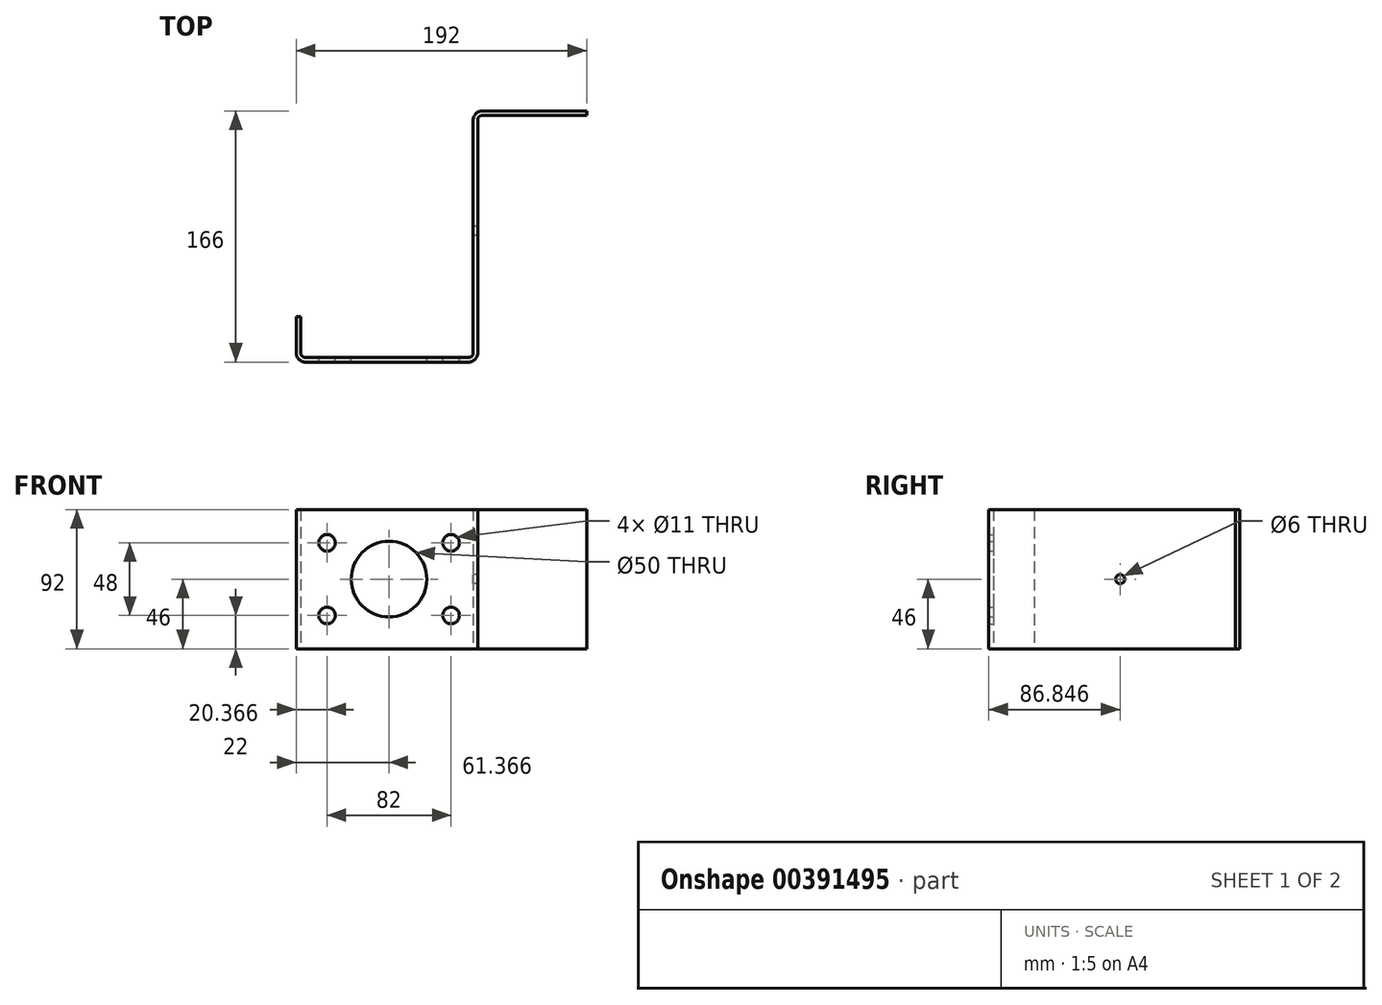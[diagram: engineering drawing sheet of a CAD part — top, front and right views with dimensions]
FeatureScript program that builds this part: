
annotation { "Feature Type Name" : "Feature", "Feature Type Description" : "" }
export const myFeature = defineFeature(function(context is Context, id is Id, definition is map)
    precondition{}
    {
        {
            var Q0;
            Q0=qCreatedBy(makeId("Top.planeOp"),FACE);
            var sketch = newSketch(context, id + "F0", { "sketchPlane" : qUnion([Q0])});
            skLineSegment(sketch, "E0.0", {"start": v(-53.85, -43.25) * mm, "end": v(-53.85, 110.75) * mm});
            skLineSegment(sketch, "E1", {"start": v(-47.85, 113.75) * mm, "end": v(21.15, 113.75) * mm});
            skLineSegment(sketch, "E2.0", {"start": v(-50.85, -43.25) * mm, "end": v(-50.85, 110.75) * mm});
            skArc(sketch, "E3.filletArc", {"start": v(-47.85, 113.75) * mm, "mid": v(-49.97, 112.88) * mm, "end": v(-50.85, 110.75) * mm});
            skLineSegment(sketch, "E4.0", {"start": v(-47.85, 116.75) * mm, "end": v(21.15, 116.75) * mm});
            skLineSegment(sketch, "E5", {"start": v(-164.85, -46.25) * mm, "end": v(-56.85, -46.25) * mm});
            skArc(sketch, "E6.filletArc", {"start": v(-56.85, -46.25) * mm, "mid": v(-54.73, -45.37) * mm, "end": v(-53.85, -43.25) * mm});
            skLineSegment(sketch, "E7", {"start": v(-170.85, -19.25) * mm, "end": v(-170.85, -43.25) * mm});
            skLineSegment(sketch, "E8.0", {"start": v(-167.85, -19.25) * mm, "end": v(-167.85, -43.25) * mm});
            skLineSegment(sketch, "E9.0", {"start": v(-164.85, -49.25) * mm, "end": v(-56.85, -49.25) * mm});
            skArc(sketch, "E10.filletArc", {"start": v(-167.85, -43.25) * mm, "mid": v(-166.97, -45.37) * mm, "end": v(-164.85, -46.25) * mm});
            skArc(sketch, "E11.filletArc", {"start": v(-170.85, -43.25) * mm, "mid": v(-169.1, -47.49) * mm, "end": v(-164.85, -49.25) * mm});
            skPoint(sketch, "E12.newPointB", {"position": v(-50.85, -50.76) * mm});
            skArc(sketch, "E12.filletArc", {"start": v(-56.85, -49.25) * mm, "mid": v(-52.61, -47.49) * mm, "end": v(-50.85, -43.25) * mm});
            skLineSegment(sketch, "E13", {"start": v(-170.85, -19.25) * mm, "end": v(-167.85, -19.25) * mm});
            skPoint(sketch, "E14.visualSharp", {"position": v(-53.85, 116.75) * mm});
            skArc(sketch, "E14.filletArc", {"start": v(-47.85, 116.75) * mm, "mid": v(-52.1, 115) * mm, "end": v(-53.85, 110.75) * mm});
            skLineSegment(sketch, "E15", {"start": v(21.15, 116.75) * mm, "end": v(21.15, 113.75) * mm});
            skSolve(sketch);
        }
        {
            var Q0;
            Q0=makeQuery(id+"F0.imprint","IMPRINT",FACE,{"disambiguationData":[TD([[makeQuery(id+"F0.imprint","IMPRINT",EDGE,{"derivedFrom":sQuery(id+"F0.wireOp",EDGE,"E0.0")}),-1.0]])]});
            extrude(context, id + "F1", {"entities" : qUnion([Q0]), "depth" : 92 * mm, "symmetric" : true});
        }
        {
            var Q0;
            Q0=makeQuery(id+"F1.opExtrude","SWEPT_FACE",FACE,{"disambiguationData":[OSD([sQuery(id+"F0.wireOp",EDGE,"E9.0")])]});
            var sketch = newSketch(context, id + "F2", { "sketchPlane" : qUnion([Q0])});
            skLineSegment(sketch, "E16.bottom", {"start": v(-68.48, 24) * mm, "end": v(-150.48, 24) * mm, "construction": true});
            skLineSegment(sketch, "E16.top", {"start": v(-68.48, -24) * mm, "end": v(-150.48, -24) * mm, "construction": true});
            skLineSegment(sketch, "E16.left", {"start": v(-68.48, 24) * mm, "end": v(-68.48, -24) * mm, "construction": true});
            skLineSegment(sketch, "E16.right", {"start": v(-150.48, 24) * mm, "end": v(-150.48, -24) * mm, "construction": true});
            skPoint(sketch, "E16.middle", {"position": v(-109.48, 0) * mm});
            skSolve(sketch);
        }
        {
            var Q0;
            Q0=sQuery(id+"F2.wireOp",VERTEX,"E16.right.start");
            var Q1;
            Q1=sQuery(id+"F2.wireOp",VERTEX,"E16.left.start");
            var Q2;
            Q2=sQuery(id+"F2.wireOp",VERTEX,"E16.left.end");
            var Q3;
            Q3=sQuery(id+"F2.wireOp",VERTEX,"E16.top.end");
            var Q4;
            Q4=makeQuery(id+"F1.opExtrude","SWEPT_BODY",BODY,{"disambiguationData":[OSD([sQuery(id+"F0.wireOp",EDGE,"E0.0"),sQuery(id+"F0.wireOp",EDGE,"E1"),sQuery(id+"F0.wireOp",EDGE,"E2.0"),sQuery(id+"F0.wireOp",EDGE,"E3.filletArc"),sQuery(id+"F0.wireOp",EDGE,"E4.0"),sQuery(id+"F0.wireOp",EDGE,"E5"),sQuery(id+"F0.wireOp",EDGE,"E6.filletArc"),sQuery(id+"F0.wireOp",EDGE,"E7"),sQuery(id+"F0.wireOp",EDGE,"E8.0"),sQuery(id+"F0.wireOp",EDGE,"E9.0"),sQuery(id+"F0.wireOp",EDGE,"E10.filletArc"),sQuery(id+"F0.wireOp",EDGE,"E11.filletArc"),sQuery(id+"F0.wireOp",EDGE,"E12.filletArc"),sQuery(id+"F0.wireOp",EDGE,"E13"),sQuery(id+"F0.wireOp",EDGE,"E14.filletArc"),sQuery(id+"F0.wireOp",EDGE,"E15")])]});
            hole(context, id + "F3", {"style" : HoleStyle.SIMPLE, "endStyle" : HoleEndStyle.THROUGH, "holeDiameter" : 11 * mm, "isTappedThrough" : true, "tappedDepth" : 12 * mm, "tapClearance" : 3, "locations" : qUnion([Q0, Q1, Q2, Q3]), "scope" : qUnion([Q4]), "startStyle" : HoleStartStyle.SKETCH});
        }
        {
            var Q0;
            Q0=sQuery(id+"F2.wireOp",VERTEX,"E16.middle");
            var Q1;
            Q1=makeQuery(id+"F1.opExtrude","SWEPT_BODY",BODY,{"disambiguationData":[OSD([sQuery(id+"F0.wireOp",EDGE,"E0.0"),sQuery(id+"F0.wireOp",EDGE,"E1"),sQuery(id+"F0.wireOp",EDGE,"E2.0"),sQuery(id+"F0.wireOp",EDGE,"E3.filletArc"),sQuery(id+"F0.wireOp",EDGE,"E4.0"),sQuery(id+"F0.wireOp",EDGE,"E5"),sQuery(id+"F0.wireOp",EDGE,"E6.filletArc"),sQuery(id+"F0.wireOp",EDGE,"E7"),sQuery(id+"F0.wireOp",EDGE,"E8.0"),sQuery(id+"F0.wireOp",EDGE,"E9.0"),sQuery(id+"F0.wireOp",EDGE,"E10.filletArc"),sQuery(id+"F0.wireOp",EDGE,"E11.filletArc"),sQuery(id+"F0.wireOp",EDGE,"E12.filletArc"),sQuery(id+"F0.wireOp",EDGE,"E13"),sQuery(id+"F0.wireOp",EDGE,"E14.filletArc"),sQuery(id+"F0.wireOp",EDGE,"E15")])]});
            hole(context, id + "F4", {"style" : HoleStyle.SIMPLE, "endStyle" : HoleEndStyle.THROUGH, "holeDiameter" : 50 * mm, "isTappedThrough" : true, "tappedDepth" : 12 * mm, "tapClearance" : 3, "locations" : qUnion([Q0]), "scope" : qUnion([Q1]), "startStyle" : HoleStartStyle.SKETCH});
        }
        {
            var Q0;
            Q0=makeQuery(id+"F1.opExtrude","SWEPT_FACE",FACE,{"disambiguationData":[OSD([sQuery(id+"F0.wireOp",EDGE,"E2.0")])]});
            var sketch = newSketch(context, id + "F5", { "sketchPlane" : qUnion([Q0])});
            skLineSegment(sketch, "E17", {"start": v(37.6, -35) * mm, "end": v(37.6, 28.9) * mm, "construction": true});
            skLineSegment(sketch, "E18.bottom", {"start": v(51.6, 20) * mm, "end": v(23.6, 20) * mm});
            skLineSegment(sketch, "E18.top", {"start": v(51.6, -20) * mm, "end": v(23.6, -20) * mm});
            skLineSegment(sketch, "E18.left", {"start": v(57.6, 14) * mm, "end": v(57.6, -14) * mm});
            skLineSegment(sketch, "E18.right", {"start": v(17.6, 14) * mm, "end": v(17.6, -14) * mm});
            skPoint(sketch, "E18.middle", {"position": v(37.6, 0) * mm});
            skPoint(sketch, "E19.visualSharp", {"position": v(17.6, 20) * mm});
            skArc(sketch, "E19.filletArc", {"start": v(23.6, 20) * mm, "mid": v(19.35, 18.24) * mm, "end": v(17.6, 14) * mm});
            skPoint(sketch, "E20.visualSharp", {"position": v(57.6, 20) * mm});
            skArc(sketch, "E20.filletArc", {"start": v(57.6, 14) * mm, "mid": v(55.84, 18.24) * mm, "end": v(51.6, 20) * mm});
            skPoint(sketch, "E21.visualSharp", {"position": v(57.6, -20) * mm});
            skArc(sketch, "E21.filletArc", {"start": v(51.6, -20) * mm, "mid": v(55.84, -18.24) * mm, "end": v(57.6, -14) * mm});
            skPoint(sketch, "E22.visualSharp", {"position": v(17.6, -20) * mm});
            skArc(sketch, "E22.filletArc", {"start": v(17.6, -14) * mm, "mid": v(19.35, -18.24) * mm, "end": v(23.6, -20) * mm});
            skLineSegment(sketch, "E23.bottom", {"start": v(51.6, -17.5) * mm, "end": v(23.6, -17.5) * mm});
            skLineSegment(sketch, "E23.top", {"start": v(51.6, 17.5) * mm, "end": v(23.6, 17.5) * mm});
            skLineSegment(sketch, "E23.left", {"start": v(55.1, -14) * mm, "end": v(55.1, 14) * mm});
            skLineSegment(sketch, "E23.right", {"start": v(20.1, -14) * mm, "end": v(20.1, 14) * mm});
            skPoint(sketch, "E24.visualSharp", {"position": v(20.1, 17.5) * mm});
            skArc(sketch, "E24.filletArc", {"start": v(23.6, 17.5) * mm, "mid": v(21.12, 16.47) * mm, "end": v(20.1, 14) * mm});
            skPoint(sketch, "E25.visualSharp", {"position": v(55.1, 17.5) * mm});
            skArc(sketch, "E25.filletArc", {"start": v(55.1, 14) * mm, "mid": v(54.07, 16.47) * mm, "end": v(51.6, 17.5) * mm});
            skPoint(sketch, "E26.visualSharp", {"position": v(55.1, -17.5) * mm});
            skArc(sketch, "E26.filletArc", {"start": v(51.6, -17.5) * mm, "mid": v(54.07, -16.47) * mm, "end": v(55.1, -14) * mm});
            skPoint(sketch, "E27.visualSharp", {"position": v(20.1, -17.5) * mm});
            skArc(sketch, "E27.filletArc", {"start": v(20.1, -14) * mm, "mid": v(21.12, -16.47) * mm, "end": v(23.6, -17.5) * mm});
            skSolve(sketch);
        }
        {
            var Q0;
            Q0=sQuery(id+"F5.wireOp",EDGE,"E23.top");
            var Q1;
            Q1=sQuery(id+"F5.wireOp",EDGE,"E24.filletArc");
            var Q2;
            Q2=sQuery(id+"F5.wireOp",EDGE,"E23.right");
            var Q3;
            Q3=sQuery(id+"F5.wireOp",EDGE,"E27.filletArc");
            var Q4;
            Q4=sQuery(id+"F5.wireOp",EDGE,"E23.bottom");
            var Q5;
            Q5=sQuery(id+"F5.wireOp",EDGE,"E26.filletArc");
            var Q6;
            Q6=sQuery(id+"F5.wireOp",EDGE,"E23.left");
            var Q7;
            Q7=sQuery(id+"F5.wireOp",EDGE,"E25.filletArc");
            var Q8;
            Q8=sQuery(id+"F5.wireOp",EDGE,"E20.filletArc");
            var Q9;
            Q9=sQuery(id+"F5.wireOp",EDGE,"E18.bottom");
            var Q10;
            Q10=sQuery(id+"F5.wireOp",EDGE,"E19.filletArc");
            var Q11;
            Q11=sQuery(id+"F5.wireOp",EDGE,"E18.right");
            var Q12;
            Q12=sQuery(id+"F5.wireOp",EDGE,"E22.filletArc");
            var Q13;
            Q13=sQuery(id+"F5.wireOp",EDGE,"E18.top");
            var Q14;
            Q14=sQuery(id+"F5.wireOp",EDGE,"E21.filletArc");
            var Q15;
            Q15=sQuery(id+"F5.wireOp",EDGE,"E18.left");
            extrude(context, id + "F6", {"bodyType" : ExtendedToolBodyType.SURFACE, "surfaceEntities" : qUnion([Q0, Q1, Q2, Q3, Q4, Q5, Q6, Q7, Q8, Q9, Q10, Q11, Q12, Q13, Q14, Q15]), "depth" : 250 * mm});
        }
        {
            var Q0;
            Q0=sQuery(id+"F5.wireOp",VERTEX,"E18.middle");
            var Q1;
            Q1=makeQuery(id+"F1.opExtrude","SWEPT_BODY",BODY,{"disambiguationData":[OSD([sQuery(id+"F0.wireOp",EDGE,"E0.0"),sQuery(id+"F0.wireOp",EDGE,"E1"),sQuery(id+"F0.wireOp",EDGE,"E2.0"),sQuery(id+"F0.wireOp",EDGE,"E3.filletArc"),sQuery(id+"F0.wireOp",EDGE,"E4.0"),sQuery(id+"F0.wireOp",EDGE,"E5"),sQuery(id+"F0.wireOp",EDGE,"E6.filletArc"),sQuery(id+"F0.wireOp",EDGE,"E7"),sQuery(id+"F0.wireOp",EDGE,"E8.0"),sQuery(id+"F0.wireOp",EDGE,"E9.0"),sQuery(id+"F0.wireOp",EDGE,"E10.filletArc"),sQuery(id+"F0.wireOp",EDGE,"E11.filletArc"),sQuery(id+"F0.wireOp",EDGE,"E12.filletArc"),sQuery(id+"F0.wireOp",EDGE,"E13"),sQuery(id+"F0.wireOp",EDGE,"E14.filletArc"),sQuery(id+"F0.wireOp",EDGE,"E15")])]});
            hole(context, id + "F7", {"style" : HoleStyle.SIMPLE, "endStyle" : HoleEndStyle.THROUGH, "holeDiameter" : 6 * mm, "isTappedThrough" : true, "tappedDepth" : 12 * mm, "tapClearance" : 3, "locations" : qUnion([Q0]), "scope" : qUnion([Q1]), "startStyle" : HoleStartStyle.SKETCH});
        }
    });
